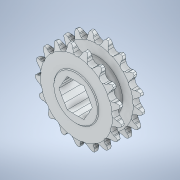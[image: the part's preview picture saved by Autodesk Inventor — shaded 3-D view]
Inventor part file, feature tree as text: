
AUTODESK INVENTOR PART (.ipt)
format: ipt  version: 2020 (Build 240168000, 168)  size: 1,026,560 bytes
history: native  units: in
note: dims shown in document units (in); Inventor stores cm internally (conversion verified against a paired STEP export)
features: chamfer x1
ambient origin geometry x8: Origin, YZ Plane, XZ Plane, XY Plane, X Axis, Y Axis, Z Axis, Center Point
bodies: Solid1 (feature_tree)
feature tree (1):
  chamfer  "Chamfer4"  [1 undecoded]
note: 1 required parameter value undecoded (feature->parameter linkage not recoverable at this tier; creation-order binding heuristic only, values carry confidence <= 0.55)
